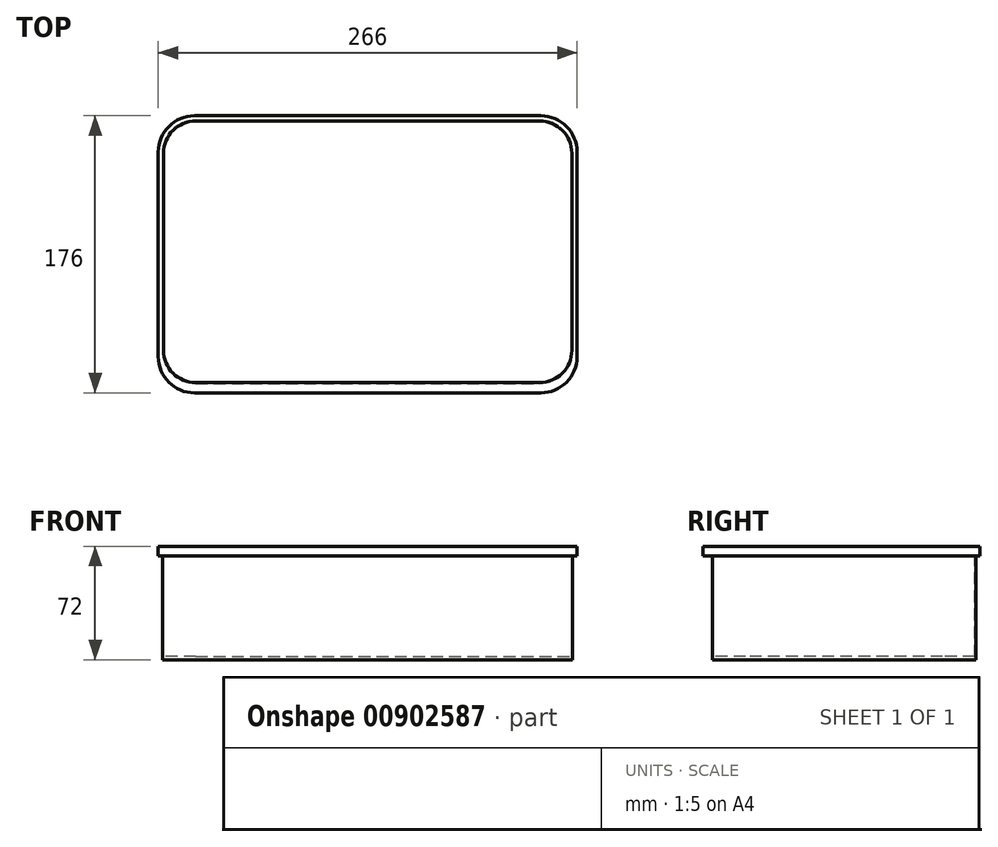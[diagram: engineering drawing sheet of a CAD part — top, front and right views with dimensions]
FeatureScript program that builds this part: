
annotation { "Feature Type Name" : "Feature", "Feature Type Description" : "" }
export const myFeature = defineFeature(function(context is Context, id is Id, definition is map)
    precondition{}
    {
        {
            var Q0;
            Q0=qCreatedBy(makeId("Top.planeOp"),FACE);
            var sketch = newSketch(context, id + "F0", { "sketchPlane" : qUnion([Q0])});
            skLineSegment(sketch, "E0.bottom", {"start": v(-120.28, 96.28) * mm, "end": v(99.72, 96.28) * mm});
            skLineSegment(sketch, "E0.left", {"start": v(-143.28, 73.28) * mm, "end": v(-143.28, -56.72) * mm});
            skLineSegment(sketch, "E0.right", {"start": v(122.72, 73.28) * mm, "end": v(122.72, -56.72) * mm});
            skPoint(sketch, "E1.visualSharp", {"position": v(-143.28, 96.28) * mm});
            skArc(sketch, "E1.filletArc", {"start": v(-120.28, 96.28) * mm, "mid": v(-136.55, 89.54) * mm, "end": v(-143.28, 73.28) * mm});
            skPoint(sketch, "E2.visualSharp", {"position": v(-143.28, -79.72) * mm});
            skArc(sketch, "E2.filletArc", {"start": v(-143.28, -56.72) * mm, "mid": v(-136.55, -72.99) * mm, "end": v(-120.28, -79.72) * mm});
            skPoint(sketch, "E3.visualSharp", {"position": v(122.72, -79.72) * mm});
            skArc(sketch, "E3.filletArc", {"start": v(99.72, -79.72) * mm, "mid": v(115.98, -72.99) * mm, "end": v(122.72, -56.72) * mm});
            skPoint(sketch, "E4.visualSharp", {"position": v(122.72, 96.28) * mm});
            skArc(sketch, "E4.filletArc", {"start": v(122.72, 73.28) * mm, "mid": v(115.98, 89.54) * mm, "end": v(99.72, 96.28) * mm});
            skLineSegment(sketch, "E5.0", {"start": v(-119.48, 93.48) * mm, "end": v(98.92, 93.48) * mm});
            skLineSegment(sketch, "E5.1", {"start": v(-140.48, 72.48) * mm, "end": v(-140.48, -52.72) * mm});
            skLineSegment(sketch, "E5.2", {"start": v(-119.48, -73.72) * mm, "end": v(98.92, -73.72) * mm});
            skLineSegment(sketch, "E5.3", {"start": v(119.92, 72.48) * mm, "end": v(119.92, -52.72) * mm});
            skPoint(sketch, "E6.visualSharp", {"position": v(-140.48, 93.48) * mm});
            skArc(sketch, "E6.filletArc", {"start": v(-119.48, 93.48) * mm, "mid": v(-134.33, 87.33) * mm, "end": v(-140.48, 72.48) * mm});
            skPoint(sketch, "E7.visualSharp", {"position": v(-140.48, -73.72) * mm});
            skArc(sketch, "E7.filletArc", {"start": v(-140.48, -52.72) * mm, "mid": v(-134.33, -67.57) * mm, "end": v(-119.48, -73.72) * mm});
            skPoint(sketch, "E8.visualSharp", {"position": v(119.92, -73.72) * mm});
            skArc(sketch, "E8.filletArc", {"start": v(98.92, -73.72) * mm, "mid": v(113.77, -67.57) * mm, "end": v(119.92, -52.72) * mm});
            skPoint(sketch, "E9.visualSharp", {"position": v(119.92, 93.48) * mm});
            skArc(sketch, "E9.filletArc", {"start": v(119.92, 72.48) * mm, "mid": v(113.77, 87.33) * mm, "end": v(98.92, 93.48) * mm});
            skLineSegment(sketch, "E10", {"start": v(-120.28, -79.72) * mm, "end": v(99.72, -79.72) * mm});
            skSolve(sketch);
        }
        {
            var Q0;
            Q0=makeQuery(id+"F0.imprint","IMPRINT",FACE,{"disambiguationData":[TD([[makeQuery(id+"F0.imprint","IMPRINT",EDGE,{"derivedFrom":sQuery(id+"F0.wireOp",EDGE,"E5.0")}),-1.0]])]});
            extrude(context, id + "F1", {"entities" : qUnion([Q0]), "oppositeDirection" : true, "depth" : 72 * mm, "offsetDistance" : 25 * mm});
        }
        {
            var Q0;
            Q0=makeQuery(id+"F0.imprint","IMPRINT",FACE,{"disambiguationData":[TD([[makeQuery(id+"F0.imprint","IMPRINT",EDGE,{"derivedFrom":sQuery(id+"F0.wireOp",EDGE,"E0.bottom")}),-1.0]])]});
            extrude(context, id + "F2", {"entities" : qUnion([Q0]), "operationType" : NewBodyOperationType.ADD, "oppositeDirection" : true, "depth" : 6 * mm, "offsetDistance" : 25 * mm});
        }
        {
            var Q0;
            Q0=makeQuery(id+"F0.imprint","IMPRINT",FACE,{"disambiguationData":[TD([[makeQuery(id+"F0.imprint","IMPRINT",EDGE,{"derivedFrom":sQuery(id+"F0.wireOp",EDGE,"E5.0")}),-1.0]])]});
            var sketch = newSketch(context, id + "F3", { "sketchPlane" : qUnion([Q0])});
            skArc(sketch, "E11.0", {"start": v(-119.48, 92.98) * mm, "mid": v(-133.98, 86.97) * mm, "end": v(-139.98, 72.48) * mm});
            skLineSegment(sketch, "E11.1", {"start": v(-139.98, 72.48) * mm, "end": v(-139.98, -52.72) * mm});
            skLineSegment(sketch, "E11.2", {"start": v(-119.48, 92.98) * mm, "end": v(98.92, 92.98) * mm});
            skArc(sketch, "E11.3", {"start": v(-139.98, -52.72) * mm, "mid": v(-133.98, -67.22) * mm, "end": v(-119.48, -73.22) * mm});
            skArc(sketch, "E11.4", {"start": v(119.42, 72.48) * mm, "mid": v(113.41, 86.97) * mm, "end": v(98.92, 92.98) * mm});
            skLineSegment(sketch, "E11.5", {"start": v(119.42, 72.48) * mm, "end": v(119.42, -52.72) * mm});
            skArc(sketch, "E11.6", {"start": v(98.92, -73.22) * mm, "mid": v(113.41, -67.22) * mm, "end": v(119.42, -52.72) * mm});
            skLineSegment(sketch, "E11.7", {"start": v(-119.48, -73.22) * mm, "end": v(98.92, -73.22) * mm});
            skSolve(sketch);
        }
        {
            var Q0;
            Q0=makeQuery(id+"F3.imprint","IMPRINT",FACE,{"disambiguationData":[TD([[makeQuery(id+"F3.imprint","IMPRINT",EDGE,{"derivedFrom":sQuery(id+"F3.wireOp",EDGE,"E11.0")}),1.0]])]});
            extrude(context, id + "F4", {"entities" : qUnion([Q0]), "operationType" : NewBodyOperationType.REMOVE, "oppositeDirection" : true, "depth" : 70 * mm, "offsetDistance" : 25 * mm});
        }
    });
